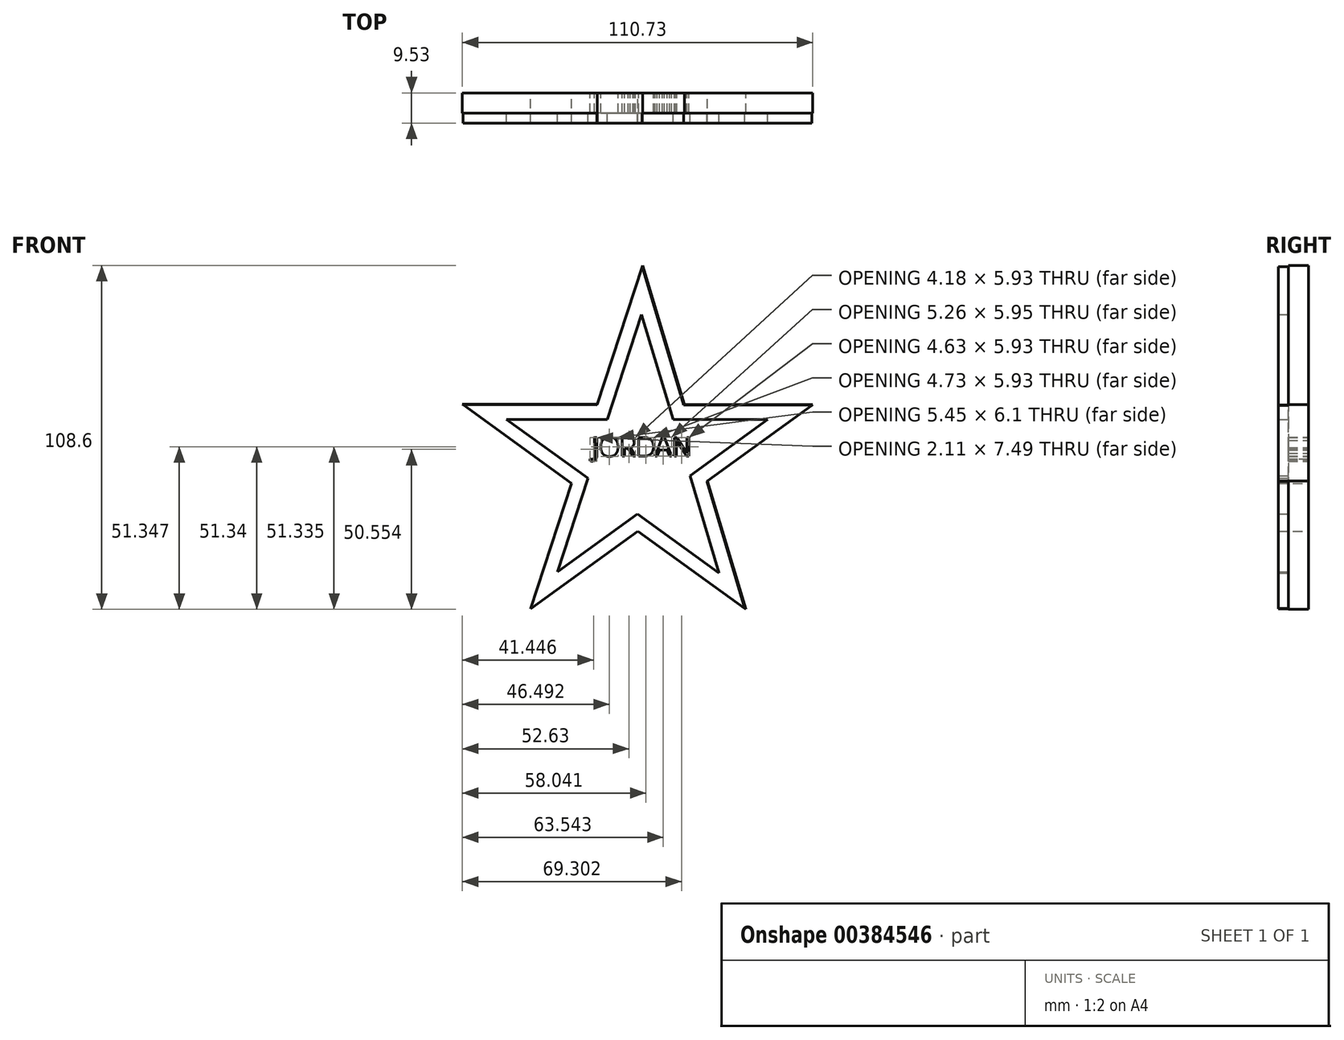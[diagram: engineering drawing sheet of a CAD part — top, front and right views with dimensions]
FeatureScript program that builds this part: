
annotation { "Feature Type Name" : "Feature", "Feature Type Description" : "" }
export const myFeature = defineFeature(function(context is Context, id is Id, definition is map)
    precondition{}
    {
        {
            var Q0;
            Q0=qCreatedBy(makeId("Front.planeOp"),FACE);
            var sketch = newSketch(context, id + "F0", { "sketchPlane" : qUnion([Q0])});
            skPoint(sketch, "E0.0.midPoint", {"position": v(-27.1, -41.2) * mm});
            skPoint(sketch, "E1.0.midPoint", {"position": v(59.14, -6.27) * mm});
            skLineSegment(sketch, "E2", {"start": v(69.7, 26.07) * mm, "end": v(29.15, 26.12) * mm});
            skLineSegment(sketch, "E3", {"start": v(-41.04, 26.21) * mm, "end": v(-6.48, 1.21) * mm});
            skLineSegment(sketch, "E4", {"start": v(48.58, -38.6) * mm, "end": v(36.4, 1.95) * mm});
            skLineSegment(sketch, "E5", {"start": v(15.97, 70) * mm, "end": v(1.66, 26.16) * mm});
            skLineSegment(sketch, "E6", {"start": v(-19.44, -38.51) * mm, "end": v(14.48, -13.94) * mm});
            skText(sketch, "E7", { "text": "JORDAN", "fontName": "OpenSans-Regular.ttf"});
            skPoint(sketch, "E7.firstSnap0", {"position": v(-1.74, 15.74) * mm});
            skLineSegment(sketch, "E8.trimOffspring", {"start": v(29.15, 26.12) * mm, "end": v(15.97, 70) * mm});
            skLineSegment(sketch, "E9.trimOffspring", {"start": v(1.66, 26.16) * mm, "end": v(-41.04, 26.21) * mm});
            skLineSegment(sketch, "E10.trimOffspring", {"start": v(-6.48, 1.21) * mm, "end": v(-19.44, -38.51) * mm});
            skLineSegment(sketch, "E11.trimOffspring", {"start": v(14.48, -13.94) * mm, "end": v(48.58, -38.6) * mm});
            skLineSegment(sketch, "E12.trimOffspring", {"start": v(36.4, 1.95) * mm, "end": v(69.7, 26.07) * mm});
            const initialGuessF0  = {"E7": [0, 0.00976, 1, 0, 0.00598]};
            skSetInitialGuess(sketch, initialGuessF0);
            skSolve(sketch);
        }
        {
            var Q0;
            {var subQ1=sQuery(id+"F0.wireOp",EDGE,"E2");var subQ5=sQuery(id+"F0.wireOp",EDGE,"E4");var subQ6=makeQuery(id+"F0.imprint","INTERSECT",VERTEX,{"derivedFrom":[subQ1,subQ5]});Q0=makeQuery(id+"F0.imprint","IMPRINT",FACE,{"disambiguationData":[TD([[makeQuery(id+"F0.imprint","IMPRINT",EDGE,{"disambiguationData":[TD([[subQ6,-1.0]])],"derivedFrom":subQ1}),1.0]])]});}
            var Q1;
            {var subQ0=sQuery(id+"F0.wireOp",EDGE,"E5");var subQ1=sQuery(id+"F0.wireOp",EDGE,"E3");var subQ2=makeQuery(id+"F0.imprint","INTERSECT",VERTEX,{"derivedFrom":[subQ1,subQ0]});Q1=makeQuery(id+"F0.imprint","IMPRINT",FACE,{"disambiguationData":[TD([[makeQuery(id+"F0.imprint","IMPRINT",EDGE,{"disambiguationData":[TD([[subQ2,-1.0]])],"derivedFrom":subQ1}),-1.0]])]});}
            var Q2;
            {var subQ0=sQuery(id+"F0.wireOp",EDGE,"E4");var subQ1=sQuery(id+"F0.wireOp",EDGE,"E3");var subQ2=makeQuery(id+"F0.imprint","INTERSECT",VERTEX,{"derivedFrom":[subQ1,subQ0]});Q2=makeQuery(id+"F0.imprint","IMPRINT",FACE,{"disambiguationData":[TD([[makeQuery(id+"F0.imprint","IMPRINT",EDGE,{"disambiguationData":[TD([[subQ2,1.0]])],"derivedFrom":subQ1}),1.0]])]});}
            var Q3;
            {var subQ0=sQuery(id+"F0.wireOp",EDGE,"E6");var subQ1=sQuery(id+"F0.wireOp",EDGE,"E2");var subQ2=makeQuery(id+"F0.imprint","INTERSECT",VERTEX,{"derivedFrom":[subQ1,subQ0]});Q3=makeQuery(id+"F0.imprint","IMPRINT",FACE,{"disambiguationData":[TD([[makeQuery(id+"F0.imprint","IMPRINT",EDGE,{"disambiguationData":[TD([[subQ2,-1.0]])],"derivedFrom":subQ1}),1.0]])]});}
            var Q4;
            {var subQ0=sQuery(id+"F0.wireOp",EDGE,"E4");var subQ1=sQuery(id+"F0.wireOp",EDGE,"E2");var subQ2=makeQuery(id+"F0.imprint","INTERSECT",VERTEX,{"derivedFrom":[subQ1,subQ0]});Q4=makeQuery(id+"F0.imprint","IMPRINT",FACE,{"disambiguationData":[TD([[makeQuery(id+"F0.imprint","IMPRINT",EDGE,{"disambiguationData":[TD([[subQ2,-1.0]])],"derivedFrom":subQ1}),-1.0]])]});}
            var Q5;
            {var subQ0=sQuery(id+"F0.wireOp",EDGE,"E3");var subQ1=sQuery(id+"F0.wireOp",EDGE,"E2");var subQ2=makeQuery(id+"F0.imprint","INTERSECT",VERTEX,{"derivedFrom":[subQ1,subQ0]});Q5=makeQuery(id+"F0.imprint","IMPRINT",FACE,{"disambiguationData":[TD([[makeQuery(id+"F0.imprint","IMPRINT",EDGE,{"disambiguationData":[TD([[subQ2,1.0]])],"derivedFrom":subQ1}),1.0]])]});}
            extrude(context, id + "F1", {"entities" : qUnion([Q0, Q1, Q2, Q3, Q4, Q5]), "depth" : 6.35 * mm});
        }
        {
            var Q0;
            Q0=makeQuery(id+"F1.opExtrude","CAP_FACE",FACE,{"disambiguationData":[OSD([sQuery(id+"F0.wireOp",EDGE,"E2"),sQuery(id+"F0.wireOp",EDGE,"E3"),sQuery(id+"F0.wireOp",EDGE,"E4"),sQuery(id+"F0.wireOp",EDGE,"E5"),sQuery(id+"F0.wireOp",EDGE,"E6"),sQuery(id+"F0.wireOp",EDGE,"E7.sketch_text.stroke-0"),sQuery(id+"F0.wireOp",EDGE,"E7.sketch_text.stroke-1"),sQuery(id+"F0.wireOp",EDGE,"E7.sketch_text.stroke-2"),sQuery(id+"F0.wireOp",EDGE,"E7.sketch_text.stroke-3"),sQuery(id+"F0.wireOp",EDGE,"E7.sketch_text.stroke-4"),sQuery(id+"F0.wireOp",EDGE,"E7.sketch_text.stroke-5"),sQuery(id+"F0.wireOp",EDGE,"E7.sketch_text.stroke-6"),sQuery(id+"F0.wireOp",EDGE,"E7.sketch_text.stroke-7"),sQuery(id+"F0.wireOp",EDGE,"E7.sketch_text.stroke-8"),sQuery(id+"F0.wireOp",EDGE,"E7.sketch_text.stroke-9"),sQuery(id+"F0.wireOp",EDGE,"E7.sketch_text.stroke-10"),sQuery(id+"F0.wireOp",EDGE,"E7.sketch_text.stroke-11"),sQuery(id+"F0.wireOp",EDGE,"E7.sketch_text.stroke-12"),sQuery(id+"F0.wireOp",EDGE,"E7.sketch_text.stroke-13"),sQuery(id+"F0.wireOp",EDGE,"E7.sketch_text.stroke-14"),sQuery(id+"F0.wireOp",EDGE,"E7.sketch_text.stroke-15"),sQuery(id+"F0.wireOp",EDGE,"E7.sketch_text.stroke-16"),sQuery(id+"F0.wireOp",EDGE,"E7.sketch_text.stroke-17"),sQuery(id+"F0.wireOp",EDGE,"E7.sketch_text.stroke-26"),sQuery(id+"F0.wireOp",EDGE,"E7.sketch_text.stroke-27"),sQuery(id+"F0.wireOp",EDGE,"E7.sketch_text.stroke-28"),sQuery(id+"F0.wireOp",EDGE,"E7.sketch_text.stroke-29"),sQuery(id+"F0.wireOp",EDGE,"E7.sketch_text.stroke-30"),sQuery(id+"F0.wireOp",EDGE,"E7.sketch_text.stroke-31"),sQuery(id+"F0.wireOp",EDGE,"E7.sketch_text.stroke-32"),sQuery(id+"F0.wireOp",EDGE,"E7.sketch_text.stroke-33"),sQuery(id+"F0.wireOp",EDGE,"E7.sketch_text.stroke-34"),sQuery(id+"F0.wireOp",EDGE,"E7.sketch_text.stroke-35"),sQuery(id+"F0.wireOp",EDGE,"E7.sketch_text.stroke-36"),sQuery(id+"F0.wireOp",EDGE,"E7.sketch_text.stroke-44"),sQuery(id+"F0.wireOp",EDGE,"E7.sketch_text.stroke-45"),sQuery(id+"F0.wireOp",EDGE,"E7.sketch_text.stroke-46"),sQuery(id+"F0.wireOp",EDGE,"E7.sketch_text.stroke-47"),sQuery(id+"F0.wireOp",EDGE,"E7.sketch_text.stroke-48"),sQuery(id+"F0.wireOp",EDGE,"E7.sketch_text.stroke-49"),sQuery(id+"F0.wireOp",EDGE,"E7.sketch_text.stroke-50"),sQuery(id+"F0.wireOp",EDGE,"E7.sketch_text.stroke-58"),sQuery(id+"F0.wireOp",EDGE,"E7.sketch_text.stroke-59"),sQuery(id+"F0.wireOp",EDGE,"E7.sketch_text.stroke-60"),sQuery(id+"F0.wireOp",EDGE,"E7.sketch_text.stroke-61"),sQuery(id+"F0.wireOp",EDGE,"E7.sketch_text.stroke-62"),sQuery(id+"F0.wireOp",EDGE,"E7.sketch_text.stroke-63"),sQuery(id+"F0.wireOp",EDGE,"E7.sketch_text.stroke-64"),sQuery(id+"F0.wireOp",EDGE,"E7.sketch_text.stroke-65"),sQuery(id+"F0.wireOp",EDGE,"E7.sketch_text.stroke-71"),sQuery(id+"F0.wireOp",EDGE,"E7.sketch_text.stroke-72"),sQuery(id+"F0.wireOp",EDGE,"E7.sketch_text.stroke-73"),sQuery(id+"F0.wireOp",EDGE,"E7.sketch_text.stroke-74"),sQuery(id+"F0.wireOp",EDGE,"E7.sketch_text.stroke-75"),sQuery(id+"F0.wireOp",EDGE,"E7.sketch_text.stroke-76"),sQuery(id+"F0.wireOp",EDGE,"E7.sketch_text.stroke-77"),sQuery(id+"F0.wireOp",EDGE,"E7.sketch_text.stroke-78"),sQuery(id+"F0.wireOp",EDGE,"E7.sketch_text.stroke-79"),sQuery(id+"F0.wireOp",EDGE,"E7.sketch_text.stroke-80"),sQuery(id+"F0.wireOp",EDGE,"E7.sketch_text.stroke-81"),sQuery(id+"F0.wireOp",EDGE,"E7.sketch_text.stroke-82"),sQuery(id+"F0.wireOp",EDGE,"E7.sketch_text.stroke-83"),sQuery(id+"F0.wireOp",EDGE,"E7.sketch_text.stroke-84"),sQuery(id+"F0.wireOp",EDGE,"E7.sketch_text.stroke-85"),sQuery(id+"F0.wireOp",EDGE,"E8.trimOffspring"),sQuery(id+"F0.wireOp",EDGE,"E9.trimOffspring"),sQuery(id+"F0.wireOp",EDGE,"E10.trimOffspring"),sQuery(id+"F0.wireOp",EDGE,"E11.trimOffspring"),sQuery(id+"F0.wireOp",EDGE,"E12.trimOffspring")])],"isStart":false});
            var sketch = newSketch(context, id + "F2", { "sketchPlane" : qUnion([Q0])});
            skPoint(sketch, "E13.0.midPoint", {"position": v(-27.27, -41.4) * mm});
            skPoint(sketch, "E14.0.midPoint", {"position": v(58.95, -6.47) * mm});
            skLineSegment(sketch, "E15", {"start": v(69.5, 25.86) * mm, "end": v(28.96, 25.92) * mm});
            skLineSegment(sketch, "E16", {"start": v(-41.22, 26.01) * mm, "end": v(-6.66, 1.01) * mm});
            skLineSegment(sketch, "E17", {"start": v(48.4, -38.8) * mm, "end": v(36.22, 1.75) * mm});
            skLineSegment(sketch, "E18", {"start": v(15.79, 69.8) * mm, "end": v(1.48, 25.95) * mm});
            skLineSegment(sketch, "E19", {"start": v(-19.63, -38.72) * mm, "end": v(14.3, -14.14) * mm});
            skPoint(sketch, "E20.firstSnap0", {"position": v(-1.92, 15.54) * mm});
            skLineSegment(sketch, "E21.trimOffspring", {"start": v(28.96, 25.92) * mm, "end": v(15.79, 69.8) * mm});
            skLineSegment(sketch, "E22.trimOffspring", {"start": v(1.48, 25.95) * mm, "end": v(-41.22, 26.01) * mm});
            skLineSegment(sketch, "E23.trimOffspring", {"start": v(-6.66, 1.01) * mm, "end": v(-19.63, -38.72) * mm});
            skLineSegment(sketch, "E24.trimOffspring", {"start": v(14.3, -14.14) * mm, "end": v(48.4, -38.8) * mm});
            skLineSegment(sketch, "E25.trimOffspring", {"start": v(36.22, 1.75) * mm, "end": v(69.5, 25.86) * mm});
            skLineSegment(sketch, "E26.0", {"start": v(30.9, 3.54) * mm, "end": v(55.43, 21.31) * mm});
            skLineSegment(sketch, "E26.1", {"start": v(40.14, -27.19) * mm, "end": v(30.9, 3.54) * mm});
            skLineSegment(sketch, "E26.2", {"start": v(55.43, 21.31) * mm, "end": v(25.56, 21.35) * mm});
            skLineSegment(sketch, "E26.3", {"start": v(14.3, -8.5) * mm, "end": v(40.14, -27.19) * mm});
            skLineSegment(sketch, "E26.4", {"start": v(-10.91, -26.76) * mm, "end": v(14.3, -8.5) * mm});
            skLineSegment(sketch, "E26.5", {"start": v(-1.28, 2.76) * mm, "end": v(-10.91, -26.76) * mm});
            skLineSegment(sketch, "E26.6", {"start": v(25.56, 21.35) * mm, "end": v(15.6, 54.5) * mm});
            skLineSegment(sketch, "E26.7", {"start": v(15.6, 54.5) * mm, "end": v(4.8, 21.38) * mm});
            skLineSegment(sketch, "E26.8", {"start": v(4.8, 21.38) * mm, "end": v(-27.07, 21.42) * mm});
            skLineSegment(sketch, "E26.9", {"start": v(-27.07, 21.42) * mm, "end": v(-1.28, 2.76) * mm});
            skSolve(sketch);
        }
        {
            var Q0;
            Q0=makeQuery(id+"F2.imprint","IMPRINT",FACE,{"disambiguationData":[TD([[makeQuery(id+"F2.imprint","IMPRINT",EDGE,{"derivedFrom":sQuery(id+"F2.wireOp",EDGE,"E26.0")}),-1.0]])]});
            extrude(context, id + "F3", {"entities" : qUnion([Q0]), "operationType" : NewBodyOperationType.ADD, "depth" : 3.17 * mm});
        }
    });
